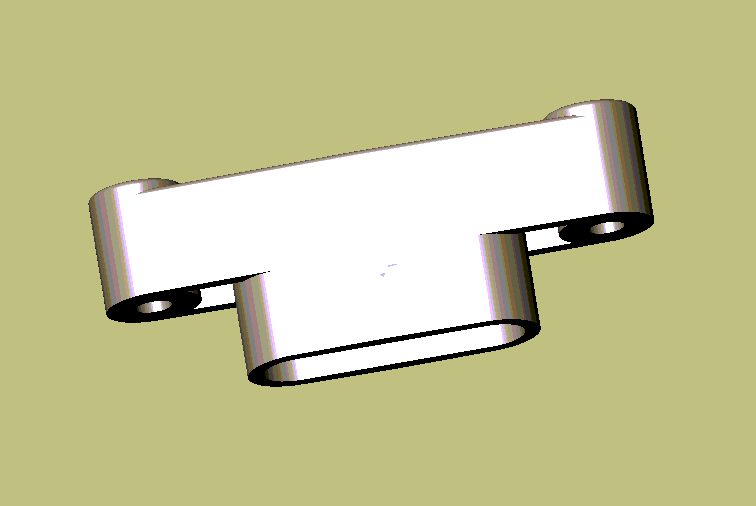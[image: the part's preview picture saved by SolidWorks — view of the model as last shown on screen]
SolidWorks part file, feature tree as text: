
SOLIDWORKS PART (.sldprt)
format: sldprt  version: not decoded by parser v0  size: 227,328 bytes
history: native  units: mm
features: sketch x8, shell x4, plane x3, cut_extrude x3, extrude x2, material x1, fillet x1 (+8 scaffold rows collapsed)
feature tree (30):
  scaffold x8  (default folders/planes/origin — collapsed)
  material  "Matériau <non spécifié>"
  plane  "Plane1"
  plane  "Plane2"
  plane  "Plane3"
  sketch  "Esquisse1"  dims[c1.D1=8.0mm c1.D2=38.0mm c1.D3=4.5mm c2.D1=19.0mm c2.D3=19.0mm c2.D4=19.0mm c2.D5=~14.008926mm]
  extrude  "Base-Extrusion"  Depth=9mm
  sketch  "Esquisse2"
  extrude  "Boss.-Extru.1"  Depth=1mm
  fillet  "Congé2"  Radius=0.5mm
  shell  "Coque1"  Thickness=1.5mm
  sketch  "Esquisse3"
  shell  "Boss.-Extru.2"  [1 undecoded]
  sketch  "Esquisse4"
  shell  "Boss.-Extru.3"  [1 undecoded]
  sketch  "Esquisse5"  dims[c1.D1=4.0mm c1.D2=4.0mm c2.D1=8.0mm]
  shell  "Boss.-Extru.4"  Thickness=15mm
  sketch  "Esquisse6"  dims[c1.D1=~7.211103mm c1.D2=~3.605551mm c2.D1=6.0mm c2.D2=6.0mm c2.D3=8.0mm c3.D1=8.0mm]
  cut_extrude  "Enlèv. mat.-Extru.1"  Depth=8mm
  sketch  "Esquisse7"  dims[c1.D1=3.0mm c1.D2=3.0mm c1.D3=3.0mm c1.D4=3.0mm c2.D2=3.0mm c2.D3=3.0mm c2.D1=3.0mm c2.D5=8.0mm c2.D6=8.0mm]
  cut_extrude  "Enlèv. mat.-Extru.2"  [1 undecoded]
  sketch  "Esquisse8"  dims[c1.D1=7.0mm c1.D2=7.0mm c2.D1=7.0mm c2.D2=7.0mm]
  cut_extrude  "Enlèv. mat.-Extru.3"  Depth=8mm
decode coverage: 12 of 18 modeling features carry decoded parameters
note: ~ marks probable driven/reference dimensions
note: 3 parameter values undecoded
summary: no parameter record found for 3 features
note: suppression state not decoded; provenance and decode notes live in map.json
